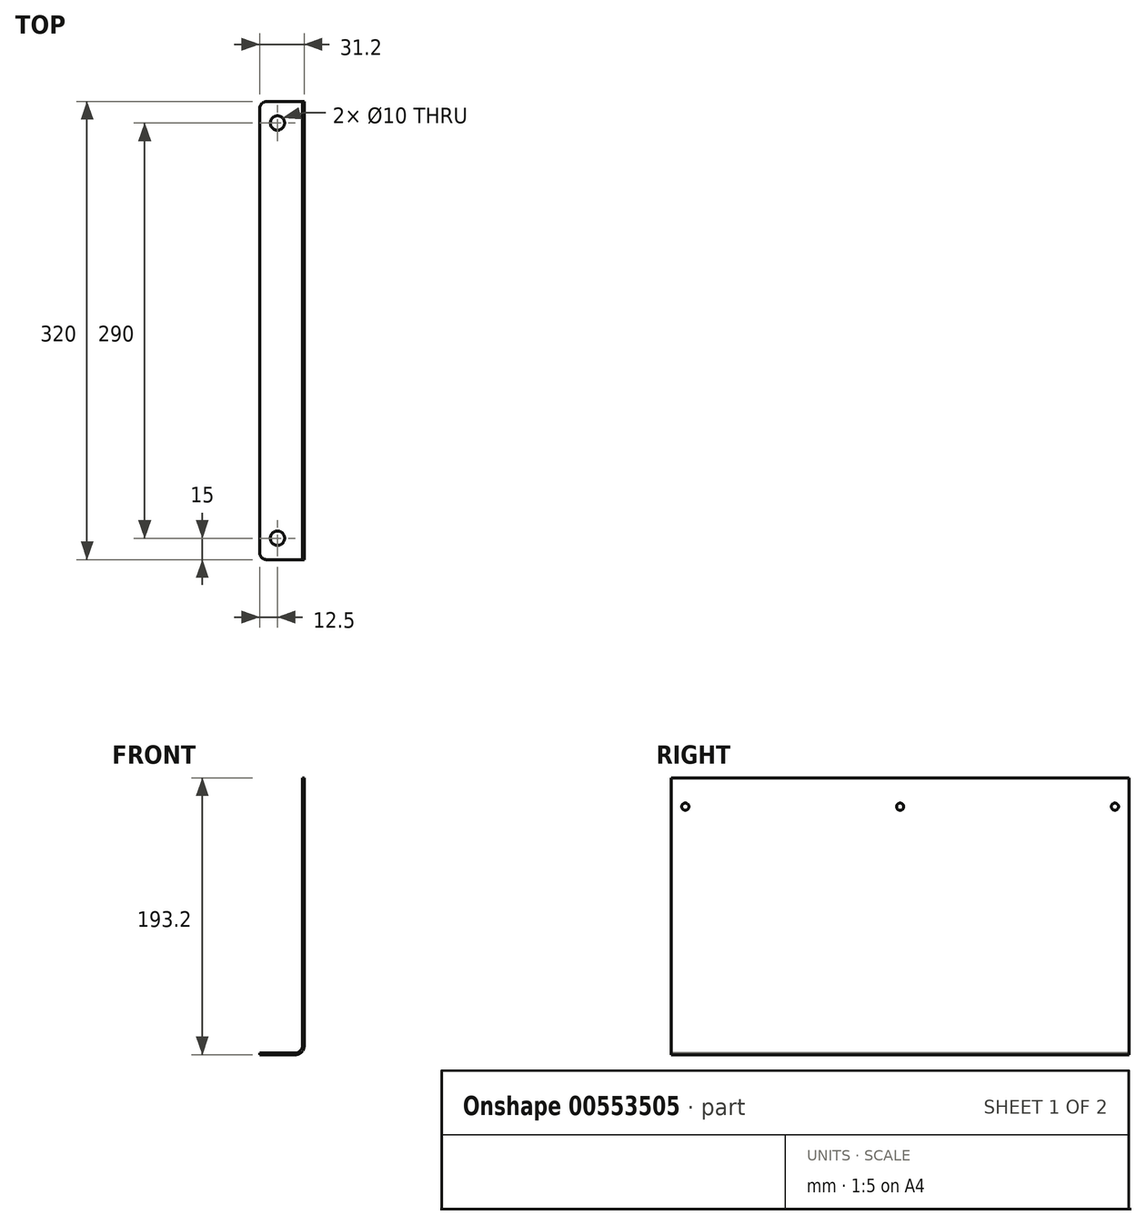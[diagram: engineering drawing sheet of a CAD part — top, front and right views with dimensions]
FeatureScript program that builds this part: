
annotation { "Feature Type Name" : "Feature", "Feature Type Description" : "" }
export const myFeature = defineFeature(function(context is Context, id is Id, definition is map)
    precondition{}
    {
        {
            var Q0;
            Q0=qCreatedBy(makeId("Front.planeOp"),FACE);
            var sketch = newSketch(context, id + "F0", { "sketchPlane" : qUnion([Q0])});
            skLineSegment(sketch, "E0", {"start": v(0, 0) * mm, "end": v(0, -187) * mm});
            skLineSegment(sketch, "E1", {"start": v(-5, -192) * mm, "end": v(-30, -192) * mm});
            skLineSegment(sketch, "E2", {"start": v(-30, -192) * mm, "end": v(-30, -193.2) * mm});
            skLineSegment(sketch, "E3", {"start": v(-30, -193.2) * mm, "end": v(-5, -193.2) * mm});
            skLineSegment(sketch, "E4", {"start": v(1.2, -187) * mm, "end": v(1.2, 0) * mm});
            skLineSegment(sketch, "E5", {"start": v(1.2, 0) * mm, "end": v(0, 0) * mm});
            skPoint(sketch, "E6.visualSharp", {"position": v(0, -192) * mm});
            skArc(sketch, "E6.filletArc", {"start": v(-5, -192) * mm, "mid": v(-1.46, -190.54) * mm, "end": v(0, -187) * mm});
            skPoint(sketch, "E7.visualSharp", {"position": v(1.2, -193.2) * mm});
            skArc(sketch, "E7.filletArc", {"start": v(-5, -193.2) * mm, "mid": v(-0.62, -191.38) * mm, "end": v(1.2, -187) * mm});
            skSolve(sketch);
        }
        {
            var Q0;
            Q0=qSketchRegion(id+"F0",true);
            extrude(context, id + "F1", {"entities" : qUnion([Q0]), "oppositeDirection" : true, "depth" : 320 * mm, "offsetDistance" : 25 * mm});
        }
        {
            var Q0;
            Q0=makeQuery(id+"F1.opExtrude","SWEPT_FACE",FACE,{"disambiguationData":[OSD([sQuery(id+"F0.wireOp",EDGE,"E1")])]});
            var sketch = newSketch(context, id + "F2", { "sketchPlane" : qUnion([Q0])});
            skCircle(sketch, "E8", {"center": v(-17.5, 305) * mm, "radius": 5 * mm});
            skCircle(sketch, "E9.0.1.0", {"center": v(-17.5, 15) * mm, "radius": 5 * mm});
            skLineSegment(sketch, "E9.direction1", {"start": v(-17.5, 305) * mm, "end": v(7.5, 305) * mm, "construction": true});
            skLineSegment(sketch, "E9.direction2", {"start": v(-17.5, 305) * mm, "end": v(-17.5, 15) * mm, "construction": true});
            skSolve(sketch);
        }
        {
            var Q0;
            Q0=qSketchRegion(id+"F2",true);
            extrude(context, id + "F3", {"entities" : qUnion([Q0]), "operationType" : NewBodyOperationType.REMOVE, "endBound" : BoundingType.UP_TO_NEXT, "oppositeDirection" : true, "depth" : 25 * mm, "offsetDistance" : 25 * mm});
        }
        {
            var Q0;
            Q0=makeQuery(id+"F1.opExtrude","CAP_EDGE",EDGE,{"disambiguationData":[OSD([sQuery(id+"F0.wireOp",EDGE,"E2")])],"isStart":false});
            var Q1;
            Q1=makeQuery(id+"F1.opExtrude","CAP_EDGE",EDGE,{"disambiguationData":[OSD([sQuery(id+"F0.wireOp",EDGE,"E2")])],"isStart":true});
            fillet(context, id + "F4", {"entities" : qUnion([Q0, Q1]), "radius" : 5 * mm, "tangentPropagation" : true, "allowEdgeOverflow" : false});
        }
        {
            var Q0;
            Q0=makeQuery(id+"F1.opExtrude","SWEPT_FACE",FACE,{"disambiguationData":[OSD([sQuery(id+"F0.wireOp",EDGE,"E4")])]});
            var sketch = newSketch(context, id + "F5", { "sketchPlane" : qUnion([Q0])});
            skCircle(sketch, "E10", {"center": v(10, -20) * mm, "radius": 2.5 * mm});
            skCircle(sketch, "E11.1.0.0", {"center": v(160, -20) * mm, "radius": 2.5 * mm});
            skCircle(sketch, "E11.2.0.0", {"center": v(310, -20) * mm, "radius": 2.5 * mm});
            skLineSegment(sketch, "E11.direction1", {"start": v(10, -20) * mm, "end": v(160, -20) * mm, "construction": true});
            skSolve(sketch);
        }
        {
            var Q0;
            Q0 = qSketchRegion(id + "F5", true);
            extrude(context, id + "F6", {"entities" : qUnion([Q0]), "operationType" : NewBodyOperationType.REMOVE, "endBound" : BoundingType.UP_TO_NEXT, "oppositeDirection" : true, "depth" : 25 * mm, "offsetDistance" : 25 * mm});
        }
    });
